# Revit family: Maxlogic Panneau Gcu
name_source: partatom
category: Fire Alarm Devices
units: mm (PartAtom-declared; Revit-internal decimal feet)

## family parameters
Cut with Voids When Loaded = No
Host = Face
Maintain Annotation Orientation = Yes
OmniClass Number = 23.85.30.21
OmniClass Title = Environmental Detection/Registration
Part Type = Normal
Room Calculation Point = No
Round Connector Dimension = Use Diameter
Shared = No

## types (7) — shared parameters
Adresse ligne 1 = Şerifali Mahallesi Kutup Sokak No:27/1-2-4 Ümraniye TR-34775 İSTANBUL
Alimentation d'externe = 220 V AC
Batterie = 2 X (12V DC 7 Ah )
Couleur = Blanc
Durée de la garantie Travail = 2
Durée de la garantie pièce rechange = 2
Hauteur Nominal = 300 mm
Largeur Nominal = 100 mm
Longeur Nominal = 400 mm
Manuel d'Installation = https://mavilielektronik.com
Manufacturer = Mavili Elektronik Ticaret A.Ş.
Matèriel Principe = Mètale Grise
Model = Maxlogic
Numéro de Fax = (+)90 216 466 45 10
Poids = 6,200 kg
Surface de Montage = Montage à Mur
Tempèrature de fonctionnement = (-5°C) - (+50°C)
URL = https://www.mavili.com.tr
Unité de durée de garantie = Ans
zero-valued in all types: Cost, Default Elevation

## per-type parameters (varying)
| type | Code de  Performance | Code de Produit | Description | Deuxième Matèriel |
| Maxlogic Panneau GCU pour système adressable module TCP/IP inclus | EN 54-4 / EN 54-18 | ML-1207.C | Maxlogic Panneau GCU pour système adressable module TCP/IP inclus | Plastique Blanche ABS |
| Maxlogic Panneau GCU pour système adressable,module GPRS inclus | EN 54-4 / EN 54-18 | ML-1207.G | Maxlogic Panneau GCU pour système adressable ,module GPRS inclus
Maxlogic Panneau GCU pour système adressable ,module GPRS inclus | Plastique Blanche  ABS |
| Maxlogic Panneau GCU pour système adressable,Module RS232/RS485 inclus | EN 54-4 / EN 54-18 | ML-1207.K | Maxlogic Panneau GCU pour système adressable,Module RS232/RS485 inclus | Plastique Blanche ABS |
| Maxlogic Panneau GCU  MODBUS  pour système adressable, 3A source d'alimentation inclus , Type B | EN 54-4 / EN 54-18 | ML-1207.MX | Panneau GCU  MODBUS  pour système adressable, 3A source d'alimentation inclus , Type B | Plastique Blanche ABS |
| Maxlogic Panneau GCU pour système adressable,Module TCP/IP,GPRS,RS-232/RS-485 inclus | EN 54-4 / EN 54-18 | ML-1207.CGK | Maxlogic Panneau GCU pour système adressable,Module TCP/IP,GPRS,RS-232/RS-485 inclus
Maxlogic Panneau GCU pour système adressable,Module TCP/IP,GPRS,RS-232/RS-485 inclus | Plastique Blanche ABS |
| Maxlogic Panneau GCU  BACNET pour système adressable, 3A source d'alimentation inclus , Type B | EN 54-4 / EN 54-18 | ML-1207.B | Panneau GCU  BACNET pour système adressable, 3A source d'alimentation inclus , Type B | Plastique Blanche ABS |
| Maxlogic Module de Communication NTP serveur |  | ML-1207.NTP | Module de Communication NTP serveur | Plastique Blanche ABS |

## geometry (parser evidence)
native form markers: Sweep x2
no freeform markers — native parametric forms only
